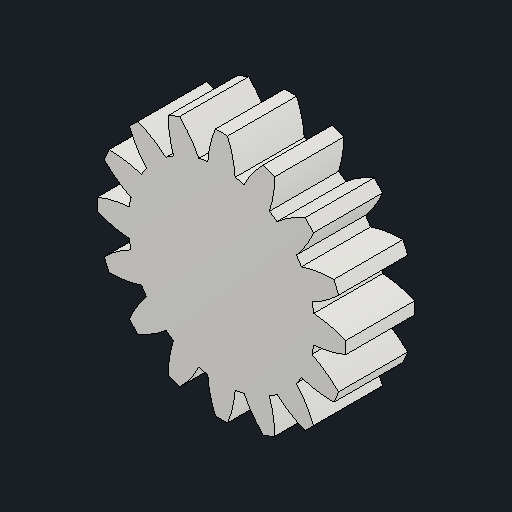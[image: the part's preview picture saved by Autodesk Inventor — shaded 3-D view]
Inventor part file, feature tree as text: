
AUTODESK INVENTOR PART (.ipt)
format: ipt  version: 2023.2 (Build 272271030, 271C)  size: 196,096 bytes
history: native  units: mm (DEFAULTED — no unit token found)
features: plane x3, other x3, sketch x2, extrude x1
ambient origin geometry x8: Origin, YZ Plane, XZ Plane, XY Plane, X Axis, Y Axis, Z Axis, Center Point
bodies: Solid1 (feature_tree)
feature tree (9):
  extrude  "Extrusion1"  Depth=10.0mm TaperAngle=0.0deg
  plane  "Work Plane2"
  plane  "Work Plane8"
  plane  "Work Plane9"
  other  "Spur Gear"
  sketch  "Sketch1"  dims[d0=36.0mm d1=10.0mm d2=0.0mm]
  sketch  "Sketch2"  dims[d3=32.0mm d4=10.0mm d5=0.0mm d16=51.0mm d17=0.0mm d34=1.963495mm d39=0.0mm d41=0.0mm d43=51.0mm d46=51.0mm d47=0.0mm d48=0.0mm]
  other  "Srf1"
  other  "Pitch Diameter"
